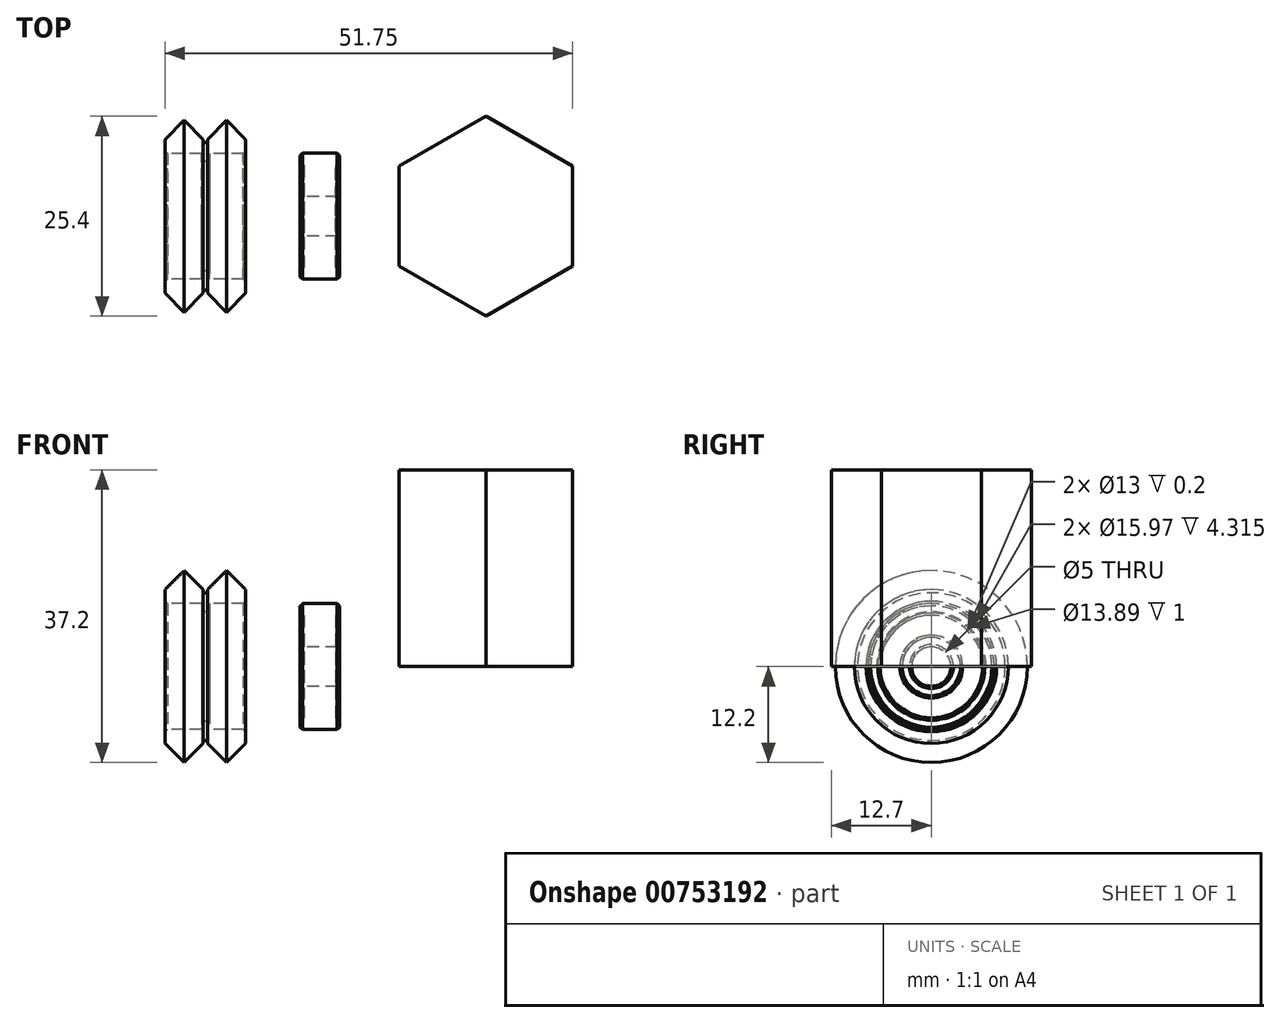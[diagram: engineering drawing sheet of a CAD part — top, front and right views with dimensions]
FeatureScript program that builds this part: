
annotation { "Feature Type Name" : "Feature", "Feature Type Description" : "" }
export const myFeature = defineFeature(function(context is Context, id is Id, definition is map)
    precondition{}
    {
        {
            var Q0;
            Q0=qCreatedBy(makeId("Front.planeOp"),FACE);
            var sketch = newSketch(context, id + "F0", { "sketchPlane" : qUnion([Q0])});
            skLineSegment(sketch, "E0", {"start": v(-13.36, 0) * mm, "end": v(13.36, 0) * mm, "construction": true});
            skLineSegment(sketch, "E1", {"start": v(0, 0) * mm, "end": v(0, 6.94) * mm, "construction": true});
            skLineSegment(sketch, "E2", {"start": v(0, 6.95) * mm, "end": v(-0.5, 6.95) * mm});
            skLineSegment(sketch, "E3", {"start": v(-0.5, 6.95) * mm, "end": v(-0.5, 7.99) * mm});
            skLineSegment(sketch, "E4", {"start": v(-0.5, 7.99) * mm, "end": v(-4.82, 7.99) * mm});
            skLineSegment(sketch, "E5", {"start": v(-4.82, 7.99) * mm, "end": v(-5.12, 8.29) * mm});
            skLineSegment(sketch, "E6", {"start": v(-5.11, 8.29) * mm, "end": v(-5.11, 9.78) * mm});
            skLineSegment(sketch, "E7", {"start": v(-5.12, 9.78) * mm, "end": v(-2.7, 12.2) * mm});
            skLineSegment(sketch, "E8", {"start": v(-2.7, 12.2) * mm, "end": v(-0.27, 9.77) * mm});
            skLineSegment(sketch, "E9", {"start": v(-0.27, 9.77) * mm, "end": v(-0.27, 9.38) * mm});
            skLineSegment(sketch, "E10", {"start": v(-0.27, 9.38) * mm, "end": v(0, 9.38) * mm});
            skLineSegment(sketch, "E11.MirrorCS", {"start": v(0.27, 9.77) * mm, "end": v(0.27, 9.38) * mm});
            skLineSegment(sketch, "E12.MirrorCS", {"start": v(2.7, 12.2) * mm, "end": v(0.28, 9.77) * mm});
            skLineSegment(sketch, "E13.MirrorCS", {"start": v(5.11, 9.78) * mm, "end": v(2.7, 12.2) * mm});
            skLineSegment(sketch, "E14.MirrorCS", {"start": v(5.12, 8.29) * mm, "end": v(5.12, 9.77) * mm});
            skLineSegment(sketch, "E15.MirrorCS", {"start": v(4.81, 7.99) * mm, "end": v(5.12, 8.29) * mm});
            skLineSegment(sketch, "E16.MirrorCS", {"start": v(0.27, 9.38) * mm, "end": v(0, 9.38) * mm});
            skLineSegment(sketch, "E17.MirrorCS", {"start": v(0.5, 7.99) * mm, "end": v(4.82, 7.99) * mm});
            skLineSegment(sketch, "E18.MirrorCS", {"start": v(0, 6.95) * mm, "end": v(0.5, 6.95) * mm});
            skLineSegment(sketch, "E19.MirrorCS", {"start": v(0.5, 6.95) * mm, "end": v(0.5, 7.99) * mm});
            skLineSegment(sketch, "E20.MirrorCS", {"start": v(-0.27, -9.38) * mm, "end": v(0, -9.38) * mm, "construction": true});
            skLineSegment(sketch, "E21.MirrorCS", {"start": v(0.27, -9.38) * mm, "end": v(0, -9.38) * mm, "construction": true});
            skLineSegment(sketch, "E22.MirrorCS", {"start": v(0.27, -9.77) * mm, "end": v(0.27, -9.38) * mm, "construction": true});
            skLineSegment(sketch, "E23.MirrorCS", {"start": v(-0.27, -9.77) * mm, "end": v(-0.27, -9.38) * mm, "construction": true});
            skLineSegment(sketch, "E24.MirrorCS", {"start": v(0, -6.95) * mm, "end": v(-0.5, -6.95) * mm, "construction": true});
            skLineSegment(sketch, "E25.MirrorCS", {"start": v(-4.81, -7.99) * mm, "end": v(-5.12, -8.29) * mm, "construction": true});
            skLineSegment(sketch, "E26.MirrorCS", {"start": v(0, -6.95) * mm, "end": v(0.5, -6.95) * mm, "construction": true});
            skLineSegment(sketch, "E27.MirrorCS", {"start": v(-2.7, -12.2) * mm, "end": v(-0.27, -9.77) * mm, "construction": true});
            skLineSegment(sketch, "E28.MirrorCS", {"start": v(2.7, -12.2) * mm, "end": v(0.28, -9.77) * mm, "construction": true});
            skLineSegment(sketch, "E29.MirrorCS", {"start": v(4.82, -7.99) * mm, "end": v(5.12, -8.29) * mm, "construction": true});
            skLineSegment(sketch, "E30.MirrorCS", {"start": v(-0.5, -7.99) * mm, "end": v(-4.82, -7.99) * mm, "construction": true});
            skLineSegment(sketch, "E31.MirrorCS", {"start": v(-5.12, -9.78) * mm, "end": v(-2.7, -12.2) * mm, "construction": true});
            skLineSegment(sketch, "E32.MirrorCS", {"start": v(5.12, -9.78) * mm, "end": v(2.7, -12.2) * mm, "construction": true});
            skLineSegment(sketch, "E33.MirrorCS", {"start": v(5.11, -8.29) * mm, "end": v(5.11, -9.77) * mm, "construction": true});
            skLineSegment(sketch, "E34.MirrorCS", {"start": v(-0.5, -6.95) * mm, "end": v(-0.5, -7.99) * mm, "construction": true});
            skLineSegment(sketch, "E35.MirrorCS", {"start": v(0.5, -7.99) * mm, "end": v(4.82, -7.99) * mm, "construction": true});
            skLineSegment(sketch, "E36.MirrorCS", {"start": v(0.5, -6.95) * mm, "end": v(0.5, -7.99) * mm, "construction": true});
            skLineSegment(sketch, "E37.MirrorCS", {"start": v(-5.12, -8.29) * mm, "end": v(-5.12, -9.77) * mm, "construction": true});
            skSolve(sketch);
        }
        {
            var Q0;
            Q0=qSketchRegion(id+"F0",true);
            var Q1;
            Q1=sQuery(id+"F0.wireOp",EDGE,"E0");
            revolve(context, id + "F1", {"surfaceOperationType" : NewSurfaceOperationType.NEW, "entities" : qUnion([Q0]), "axis" : qUnion([Q1]), "revolveType" : RevolveType.FULL});
        }
        {
            var Q0;
            Q0=qCreatedBy(makeId("Front.planeOp"),FACE);
            var sketch = newSketch(context, id + "F2", { "sketchPlane" : qUnion([Q0])});
            skLineSegment(sketch, "E38", {"start": v(11.32, 0) * mm, "end": v(17.9, 0) * mm, "construction": true});
            skLineSegment(sketch, "E39", {"start": v(17.04, 2.5) * mm, "end": v(17.04, 4) * mm});
            skLineSegment(sketch, "E40", {"start": v(17.04, 4) * mm, "end": v(16.54, 4) * mm});
            skLineSegment(sketch, "E41", {"start": v(16.54, 4) * mm, "end": v(16.54, 6.5) * mm});
            skLineSegment(sketch, "E42", {"start": v(16.54, 6.5) * mm, "end": v(17.04, 6.5) * mm});
            skLineSegment(sketch, "E43", {"start": v(17.04, 6.5) * mm, "end": v(17.04, 8) * mm});
            skLineSegment(sketch, "E44", {"start": v(17.04, 8) * mm, "end": v(14.54, 8) * mm});
            skLineSegment(sketch, "E45", {"start": v(14.54, 2.5) * mm, "end": v(14.54, 0) * mm, "construction": true});
            skPoint(sketch, "E45.endSnap0", {"position": v(14.61, 0) * mm});
            skLineSegment(sketch, "E46", {"start": v(14.54, 2.5) * mm, "end": v(17.04, 2.5) * mm});
            skLineSegment(sketch, "E47.MirrorCS", {"start": v(12.04, 4) * mm, "end": v(12.54, 4) * mm});
            skLineSegment(sketch, "E48.MirrorCS", {"start": v(12.54, 6.5) * mm, "end": v(12.04, 6.5) * mm});
            skLineSegment(sketch, "E49.MirrorCS", {"start": v(14.54, 2.5) * mm, "end": v(12.04, 2.5) * mm});
            skLineSegment(sketch, "E50.MirrorCS", {"start": v(12.04, 2.5) * mm, "end": v(12.04, 4) * mm});
            skLineSegment(sketch, "E51.MirrorCS", {"start": v(12.04, 8) * mm, "end": v(14.54, 8) * mm});
            skLineSegment(sketch, "E52.MirrorCS", {"start": v(12.54, 4) * mm, "end": v(12.54, 6.5) * mm});
            skLineSegment(sketch, "E53.MirrorCS", {"start": v(12.04, 6.5) * mm, "end": v(12.04, 8) * mm});
            skLineSegment(sketch, "E54.MirrorCS", {"start": v(16.54, -6.5) * mm, "end": v(17.04, -6.5) * mm, "construction": true});
            skLineSegment(sketch, "E55.MirrorCS", {"start": v(12.04, -4) * mm, "end": v(12.54, -4) * mm, "construction": true});
            skLineSegment(sketch, "E56.MirrorCS", {"start": v(17.04, -4) * mm, "end": v(16.54, -4) * mm, "construction": true});
            skLineSegment(sketch, "E57.MirrorCS", {"start": v(12.54, -6.5) * mm, "end": v(12.04, -6.5) * mm, "construction": true});
            skLineSegment(sketch, "E58.MirrorCS", {"start": v(14.54, -2.5) * mm, "end": v(12.04, -2.5) * mm, "construction": true});
            skLineSegment(sketch, "E59.MirrorCS", {"start": v(16.54, -4) * mm, "end": v(16.54, -6.5) * mm, "construction": true});
            skLineSegment(sketch, "E60.MirrorCS", {"start": v(12.04, -8) * mm, "end": v(14.54, -8) * mm, "construction": true});
            skLineSegment(sketch, "E61.MirrorCS", {"start": v(17.04, -8) * mm, "end": v(14.54, -8) * mm, "construction": true});
            skLineSegment(sketch, "E62.MirrorCS", {"start": v(12.04, -2.5) * mm, "end": v(12.04, -4) * mm, "construction": true});
            skLineSegment(sketch, "E63.MirrorCS", {"start": v(12.54, -4) * mm, "end": v(12.54, -6.5) * mm, "construction": true});
            skLineSegment(sketch, "E64.MirrorCS", {"start": v(17.04, -6.5) * mm, "end": v(17.04, -8) * mm, "construction": true});
            skLineSegment(sketch, "E65.MirrorCS", {"start": v(12.04, -6.5) * mm, "end": v(12.04, -8) * mm, "construction": true});
            skLineSegment(sketch, "E66.MirrorCS", {"start": v(17.04, -2.5) * mm, "end": v(17.04, -4) * mm, "construction": true});
            skLineSegment(sketch, "E67.MirrorCS", {"start": v(14.54, -2.5) * mm, "end": v(17.04, -2.5) * mm, "construction": true});
            skSolve(sketch);
        }
        {
            var Q0;
            Q0=qSketchRegion(id+"F2",true);
            var Q1;
            Q1=sQuery(id+"F2.wireOp",EDGE,"E38");
            revolve(context, id + "F3", {"surfaceOperationType" : NewSurfaceOperationType.NEW, "entities" : qUnion([Q0]), "axis" : qUnion([Q1]), "revolveType" : RevolveType.FULL});
        }
        {
            var Q0;
            Q0=makeQuery(id+"F3.opRevolve","SWEPT_EDGE",EDGE,{"disambiguationData":[OSD([sQuery(id+"F2.wireOp",EDGE,"E51.MirrorCS"),sQuery(id+"F2.wireOp",EDGE,"E53.MirrorCS")])]});
            var Q1;
            Q1=makeQuery(id+"F3.opRevolve","SWEPT_EDGE",EDGE,{"disambiguationData":[OSD([sQuery(id+"F2.wireOp",EDGE,"E43"),sQuery(id+"F2.wireOp",EDGE,"E44")])]});
            var Q2;
            Q2=makeQuery(id+"F3.opRevolve","SWEPT_EDGE",EDGE,{"disambiguationData":[OSD([sQuery(id+"F2.wireOp",EDGE,"E39"),sQuery(id+"F2.wireOp",EDGE,"E40")])]});
            var Q3;
            Q3=makeQuery(id+"F3.opRevolve","SWEPT_EDGE",EDGE,{"disambiguationData":[OSD([sQuery(id+"F2.wireOp",EDGE,"E39"),sQuery(id+"F2.wireOp",EDGE,"E46")])]});
            var Q4;
            Q4=makeQuery(id+"F3.opRevolve","SWEPT_EDGE",EDGE,{"disambiguationData":[OSD([sQuery(id+"F2.wireOp",EDGE,"E49.MirrorCS"),sQuery(id+"F2.wireOp",EDGE,"E50.MirrorCS")])]});
            var Q5;
            Q5=makeQuery(id+"F3.opRevolve","SWEPT_EDGE",EDGE,{"disambiguationData":[OSD([sQuery(id+"F2.wireOp",EDGE,"E47.MirrorCS"),sQuery(id+"F2.wireOp",EDGE,"E50.MirrorCS")])]});
            var Q6;
            Q6=makeQuery(id+"F3.opRevolve","SWEPT_EDGE",EDGE,{"disambiguationData":[OSD([sQuery(id+"F2.wireOp",EDGE,"E48.MirrorCS"),sQuery(id+"F2.wireOp",EDGE,"E53.MirrorCS")])]});
            var Q7;
            Q7=makeQuery(id+"F3.opRevolve","SWEPT_EDGE",EDGE,{"disambiguationData":[OSD([sQuery(id+"F2.wireOp",EDGE,"E42"),sQuery(id+"F2.wireOp",EDGE,"E43")])]});
            chamfer(context, id + "F4", {"entities" : qUnion([Q0, Q1, Q2, Q3, Q4, Q5, Q6, Q7]), "width" : 0.3 * mm, "tangentPropagation" : true});
        }
        {
            var Q0;
            Q0=qCreatedBy(makeId("Top.planeOp"),FACE);
            var sketch = newSketch(context, id + "F5", { "sketchPlane" : qUnion([Q0])});
            skCircle(sketch, "E68.cCircle", {"center": v(35.63, 0) * mm, "radius": 11 * mm, "construction": true});
            skLineSegment(sketch, "E68.0", {"start": v(46.63, -6.35) * mm, "end": v(35.63, -12.7) * mm});
            skLineSegment(sketch, "E68.1", {"start": v(35.63, -12.7) * mm, "end": v(24.63, -6.35) * mm});
            skLineSegment(sketch, "E68.2", {"start": v(24.63, -6.35) * mm, "end": v(24.63, 6.35) * mm});
            skLineSegment(sketch, "E68.3", {"start": v(24.63, 6.35) * mm, "end": v(35.63, 12.7) * mm});
            skLineSegment(sketch, "E68.4", {"start": v(35.63, 12.7) * mm, "end": v(46.63, 6.35) * mm});
            skLineSegment(sketch, "E68.5", {"start": v(46.63, 6.35) * mm, "end": v(46.63, -6.35) * mm});
            skPoint(sketch, "E68.0.midPoint", {"position": v(41.13, -9.53) * mm});
            skSolve(sketch);
        }
        {
            var Q0;
            Q0=makeQuery(id+"F5.imprint","IMPRINT",FACE,{"disambiguationData":[TD([[makeQuery(id+"F5.imprint","IMPRINT",EDGE,{"derivedFrom":sQuery(id+"F5.wireOp",EDGE,"E68.0")}),-1.0]])]});
            extrude(context, id + "F6", {"entities" : qUnion([Q0]), "depth" : 25 * mm, "offsetDistance" : 25 * mm});
        }
    });
